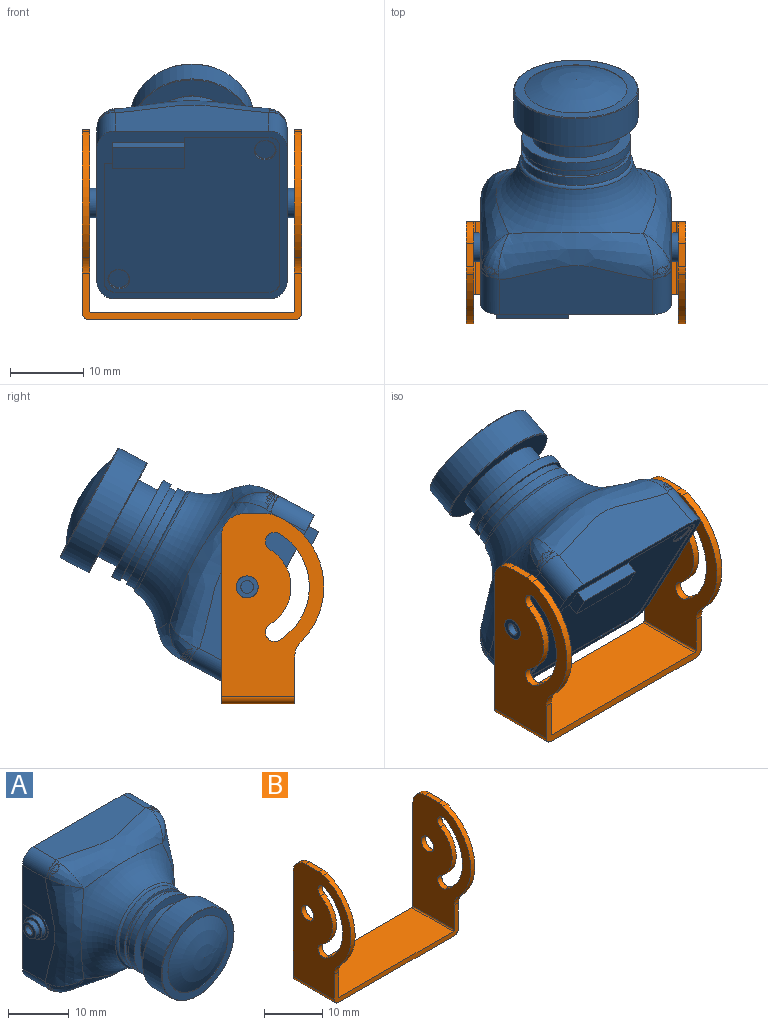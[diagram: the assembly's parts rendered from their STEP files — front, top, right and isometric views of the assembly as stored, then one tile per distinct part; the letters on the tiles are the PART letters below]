
ASSEMBLY  parts=2 mates=1
PART A: 94 faces, bbox 33.8x31.1x33.8 mm
  f0: torus R=12.35mm, axis (0,1,0), area 0mm2, adj f7,f31,f34
  f1: torus R=12.35mm, axis (0,1,0), area 0mm2, adj f8,f23,f26
  f2: torus R=12.35mm, axis (0,1,0), area 0mm2, adj f6,f28,f30
  f3: torus R=15.6mm, axis (0,1,0), area 402.5mm2, adj f5,f15,f16,f17,f18
  f4: torus R=12.35mm, axis (0,1,0), area 0mm2, adj f9,f19,f22
  f5: torus R=7.32mm, axis (0,1,0), area 33.3mm2, adj f3,f74
  f6: cylinder r=2.5mm len=5.66mm, axis (0,1,0), area 22mm2, adj f2,f10,f13,f14,f16,f18,f28,f30
  f7: cylinder r=2.5mm len=5.66mm, axis (0,1,0), area 22mm2, adj f0,f10,f11,f14,f17,f18,f31,f34
  f8: cylinder r=2.5mm len=5.66mm, axis (0,1,0), area 22mm2, adj f1,f11,f12,f14,f15,f17,f23,f26
  f9: cylinder r=2.5mm len=5.66mm, axis (0,1,0), area 22mm2, adj f4,f12,f13,f14,f15,f16,f19,f22
  f10: plane 21.01x7.56mm, normal (0,0,-1), area 137.3mm2, adj f6,f7,f14,f18
  f11: plane 21x7.56mm, normal (-1,0,0), area 109.5mm2, adj f7,f8,f14,f17,f58,f59,f60
  f12: plane 21x7.56mm, normal (0,0,1), area 137.3mm2, adj f8,f9,f14,f15
  f13: plane 21.01x7.56mm, normal (1,0,0), area 109.5mm2, adj f6,f9,f14,f16,f55,f56,f57
  f14: plane 26.25x26mm, normal (0,1,0), area 108.7mm2, adj f6,f7,f8,f9,f10,f11,f12,f13
  f15: bspline ~24.08x6.44mm, area 116mm2, adj f3,f8,f9,f12,f20,f22,f23,f24
  f16: bspline ~24.08x6.44mm, area 116mm2, adj f3,f6,f9,f13,f19,f20,f27,f28
  f17: bspline ~24.08x6.44mm, area 116mm2, adj f3,f7,f8,f11,f24,f26,f31,f32
  f18: bspline ~24.08x6.44mm, area 116mm2, adj f3,f6,f7,f10,f27,f30,f32,f34
  f19: bspline ~1.79x1.79mm, area 1.2mm2, adj f4,f9,f16,f21
  f20: bspline ~5.02x3.83mm, area 8.7mm2, adj f15,f16,f21
  f21: sphere r=2.4mm, area 2mm2, adj f19,f20,f22
  f22: bspline ~1.79x1.79mm, area 1.2mm2, adj f4,f9,f15,f21
  f23: bspline ~1.79x1.79mm, area 1.2mm2, adj f1,f8,f15,f25
  f24: bspline ~5.02x3.83mm, area 8.7mm2, adj f15,f17,f25
  f25: sphere r=2.4mm, area 2mm2, adj f23,f24,f26
  f26: bspline ~1.79x1.79mm, area 1.2mm2, adj f1,f8,f17,f25
  f27: bspline ~5.02x3.83mm, area 8.7mm2, adj f16,f18,f29
  f28: bspline ~1.79x1.79mm, area 1.2mm2, adj f2,f6,f16,f29
  f29: sphere r=2.4mm, area 2mm2, adj f27,f28,f30
  f30: bspline ~1.79x1.79mm, area 1.2mm2, adj f2,f6,f18,f29
  f31: bspline ~1.79x1.79mm, area 1.2mm2, adj f0,f7,f17,f33
  f32: bspline ~5.02x3.83mm, area 8.7mm2, adj f17,f18,f33
  f33: sphere r=2.4mm, area 2mm2, adj f31,f32,f34
  f34: bspline ~1.79x1.79mm, area 1.2mm2, adj f0,f7,f18,f33
  f35: plane 11.5x0.1mm, normal (0,0,1), area 1.1mm2, adj f14,f36,f43,f44
  f36: plane 4x1.7mm, normal (1,0,0), area 5.7mm2, adj f14,f35,f37,f44,f52,f53
  f37: plane 11x1.7mm, normal (0,0,1), area 16.9mm2, adj f14,f36,f38,f44,f51,f53
  f38: plane 18.5x0.1mm, normal (1,0,0), area 1.8mm2, adj f14,f37,f39,f44
  f39: cylinder r=1.5mm len=1.5mm, axis (0,1,0), area 0.2mm2, adj f14,f38,f40,f44
  f40: plane 21x0.1mm, normal (0,0,-1), area 2.1mm2, adj f14,f39,f41,f44
  f41: cylinder r=1.5mm len=1.5mm, axis (0,1,0), area 0.2mm2, adj f14,f40,f42,f44
  f42: plane 21x0.1mm, normal (-1,0,0), area 2.1mm2, adj f14,f41,f43,f44
  f43: cylinder r=1.5mm len=1.5mm, axis (0,1,0), area 0.2mm2, adj f14,f35,f42,f44
  f44: plane 24x24mm, normal (0,1,0), area 516.4mm2, adj f35,f36,f37,f38,f39,f40,f41,f42
  f45: cylinder r=1.4mm len=2.8mm, axis (0,1,0), area 0.9mm2, adj f46,f50
  f46: plane 2.8x2.8mm, normal (0,1,0), area 6.2mm2, adj f45
  f47: cylinder r=1.4mm len=2.8mm, axis (0,1,0), area 0.9mm2, adj f48,f49
  f48: plane 2.8x2.8mm, normal (0,1,0), area 6.2mm2, adj f47
  f49: cone r=1.4mm half-angle=45deg, axis (0,1,0), area 1.3mm2, adj f44,f47
  f50: cone r=1.4mm half-angle=45deg, axis (0,1,0), area 1.3mm2, adj f44,f45
  f51: plane 3.3x1.6mm, normal (-1,0,0), area 5.3mm2, adj f14,f37,f52,f53
  f52: plane 9.9x1.6mm, normal (0,0,-1), area 15.8mm2, adj f14,f36,f51,f53
  f53: plane 9.9x3.3mm, normal (0,1,0), area 32.7mm2, adj f36,f37,f51,f52
  f54: plane 6x5.3mm, normal (1,0,0), area 15.3mm2, adj f14,f55,f56,f57,f64
  f55: cylinder r=2.5mm len=5mm, axis (-1,0,0), area 1mm2, adj f13,f54,f56,f57
  f56: plane 3.61x0.15mm, normal (0,-0.04,1), area 0.5mm2, adj f13,f14,f54,f55
  f57: plane 3.61x0.15mm, normal (0,-0.04,-1), area 0.5mm2, adj f13,f14,f54,f55
  f58: plane 3.61x0.15mm, normal (0,-0.04,-1), area 0.5mm2, adj f11,f14,f60,f61
  f59: plane 3.61x0.15mm, normal (0,-0.04,1), area 0.5mm2, adj f11,f14,f60,f61
  f60: cylinder r=2.5mm len=5mm, axis (-1,0,0), area 1mm2, adj f11,f58,f59,f61
  f61: plane 6x5.3mm, normal (-1,0,0), area 15.3mm2, adj f14,f58,f59,f60,f63
  f62: plane 4x4mm, normal (-1,0,0), area 5.5mm2, adj f63,f71
  f63: cylinder r=2mm len=4mm, axis (-1,0,0), area 11mm2, adj f61,f62
  f64: cylinder r=2mm len=4mm, axis (-1,0,0), area 11mm2, adj f54,f65
  f65: plane 4x4mm, normal (1,0,0), area 5.5mm2, adj f64,f68
  f66: cylinder r=0.88mm len=1.75mm, axis (-1,0,0), area 5.5mm2, adj f67,f69
  f67: plane 3x3mm, normal (1,0,0), area 4.7mm2, adj f66,f68
  f68: cylinder r=1.5mm len=3mm, axis (-1,0,0), area 9.4mm2, adj f65,f67
  f69: plane 1.75x1.75mm, normal (1,0,0), area 2.4mm2, adj f66
  f70: cylinder r=0.88mm len=1.75mm, axis (-1,0,0), area 5.5mm2, adj f72,f73
  f71: cylinder r=1.5mm len=3mm, axis (-1,0,0), area 9.4mm2, adj f62,f72
  f72: plane 3x3mm, normal (-1,0,0), area 4.7mm2, adj f70,f71
  f73: plane 1.75x1.75mm, normal (-1,0,0), area 2.4mm2, adj f70
  f74: plane 14.9x14.9mm, normal (0,1,0), area 6mm2, adj f5,f75
  f75: cylinder r=7.45mm len=14.9mm, axis (0,1,0), area 58.5mm2, adj f74,f77
  f76: plane 14.9x14.9mm, normal (0,1,0), area 20.4mm2, adj f78,f86
  f77: plane 14.9x14.9mm, normal (0,-1,0), area 20.4mm2, adj f75,f78
  f78: cylinder r=7mm len=14mm, axis (0,-1,0), area 44mm2, adj f76,f77
  f79: sphere r=16mm, area 162.1mm2, adj f80
  f80: cylinder r=7mm len=14mm, axis (0,-1,0), area 4.4mm2, adj f79,f81
  f81: plane 16.8x16.8mm, normal (0,-1,0), area 67.7mm2, adj f80,f88
  f82: cylinder r=8.5mm len=17mm, axis (0,1,0), area 229.7mm2, adj f87,f88
  f83: plane 16.8x16.8mm, normal (0,1,0), area 111.4mm2, adj f84,f87
  f84: cylinder r=5.92mm len=11.85mm, axis (0,1,0), area 111.7mm2, adj f83,f85
  f85: plane 14.9x14.9mm, normal (0,-1,0), area 64.1mm2, adj f84,f86
  f86: cylinder r=7.45mm len=14.9mm, axis (0,1,0), area 58.5mm2, adj f76,f85
  f87: torus R=8.4mm, axis (0,-1,0), area 8.4mm2, adj f82,f83
  f88: torus R=8.4mm, axis (0,-1,0), area 8.4mm2, adj f81,f82
  f89: plane 11.15x3.93mm, normal (0,-1,0), area 31.9mm2, adj f91,f92
  f90: plane 11.15x3.93mm, normal (0,-1,0), area 31.9mm2, adj f91,f92
  f91: cylinder r=2.5mm len=11.15mm, axis (-1,0,0), area 51.7mm2, adj f89,f90,f92
  f92: cylinder r=5.92mm len=12mm, axis (0,-1,0), area 446.7mm2, adj f89,f90,f91,f93
  f93: plane 11.85x11.85mm, normal (0,1,0), area 110.3mm2, adj f92
PART B: 32 faces, bbox 30x14x26 mm
  f0: plane 3.19x1mm, normal (0,0,1), area 3.2mm2, adj f13,f22,f24,f29
  f1: cylinder r=3mm len=1.08mm, axis (-1,0,0), area 1.1mm2, adj f2,f12,f23,f28
  f2: cylinder r=10.5mm len=17.26mm, axis (-1,0,0), area 20.9mm2, adj f1,f3,f23,f28
  f3: cylinder r=3mm len=2.13mm, axis (-1,0,0), area 2.4mm2, adj f2,f4,f23,f28
  f4: plane 30x6.41mm, normal (0,-1,0), area 40.4mm2, adj f3,f15,f16,f23,f24,f25,f26,f27
  f5: plane 30x23mm, normal (0,1,0), area 73.6mm2, adj f11,f16,f22,f23,f24,f25,f26,f27
  f6: cylinder r=8.5mm len=14.55mm, axis (-1,0,0), area 17.5mm2, adj f7,f9,f23,f28
  f7: cylinder r=1.25mm len=2.32mm, axis (-1,0,0), area 3.9mm2, adj f6,f8,f23,f28
  f8: cylinder r=6mm len=10.27mm, axis (-1,0,0), area 12.3mm2, adj f7,f9,f23,f28
  f9: cylinder r=1.25mm len=2.32mm, axis (-1,0,0), area 3.9mm2, adj f6,f8,f23,f28
  f10: cylinder r=1.5mm len=3mm, axis (-1,0,0), area 9.4mm2, adj f23,f28
  f11: cylinder r=3mm len=3mm, axis (-1,0,0), area 4.7mm2, adj f5,f12,f23,f28
  f12: plane 3.19x1mm, normal (0,0,1), area 3.2mm2, adj f1,f11,f23,f28
  f13: cylinder r=3mm len=1.08mm, axis (-1,0,0), area 1.1mm2, adj f0,f14,f24,f29
  f14: cylinder r=10.5mm len=17.26mm, axis (-1,0,0), area 20.9mm2, adj f13,f15,f24,f29
  f15: cylinder r=3mm len=2.13mm, axis (-1,0,0), area 2.4mm2, adj f4,f14,f24,f29
  f16: plane 28x10mm, normal (0,0,-1), area 280mm2, adj f4,f5,f25,f26
  f17: cylinder r=8.5mm len=14.55mm, axis (-1,0,0), area 17.5mm2, adj f18,f20,f24,f29
  f18: cylinder r=1.25mm len=2.32mm, axis (-1,0,0), area 3.9mm2, adj f17,f19,f24,f29
  f19: cylinder r=6mm len=10.27mm, axis (-1,0,0), area 12.3mm2, adj f18,f20,f24,f29
  f20: cylinder r=1.25mm len=2.32mm, axis (-1,0,0), area 3.9mm2, adj f17,f19,f24,f29
  f21: cylinder r=1.5mm len=3mm, axis (-1,0,0), area 9.4mm2, adj f24,f29
  f22: cylinder r=3mm len=3mm, axis (-1,0,0), area 4.7mm2, adj f0,f5,f24,f29
  f23: plane 25x14mm, normal (1,0,0), area 242.6mm2, adj f1,f2,f3,f4,f5,f6,f7,f8
  f24: plane 25x14mm, normal (-1,0,0), area 242.6mm2, adj f0,f4,f5,f13,f14,f15,f17,f18
  f25: cylinder r=1mm len=10mm, axis (0,1,0), area 15.7mm2, adj f4,f5,f16,f24
  f26: cylinder r=1mm len=10mm, axis (0,-1,0), area 15.7mm2, adj f4,f5,f16,f23
  f27: plane 27.5x10mm, normal (0,0,1), area 275mm2, adj f4,f5,f30,f31
  f28: plane 24.75x14mm, normal (-1,0,0), area 240.1mm2, adj f1,f2,f3,f4,f5,f6,f7,f8
  f29: plane 24.75x14mm, normal (1,0,0), area 240.1mm2, adj f0,f4,f5,f13,f14,f15,f17,f18
  f30: cylinder r=0.25mm len=10mm, axis (0,1,0), area 3.9mm2, adj f4,f5,f27,f28
  f31: cylinder r=0.25mm len=10mm, axis (0,-1,0), area 3.9mm2, adj f4,f5,f27,f29
PLACE A rot(axis=(-1,0,0),151.9deg) t=(0,-1.59,1.35)mm
PLACE B at identity fixed
MATE revolute A.f55 <-> B.f2  axis (-1,0,0) through (-14,1.5,3)mm
